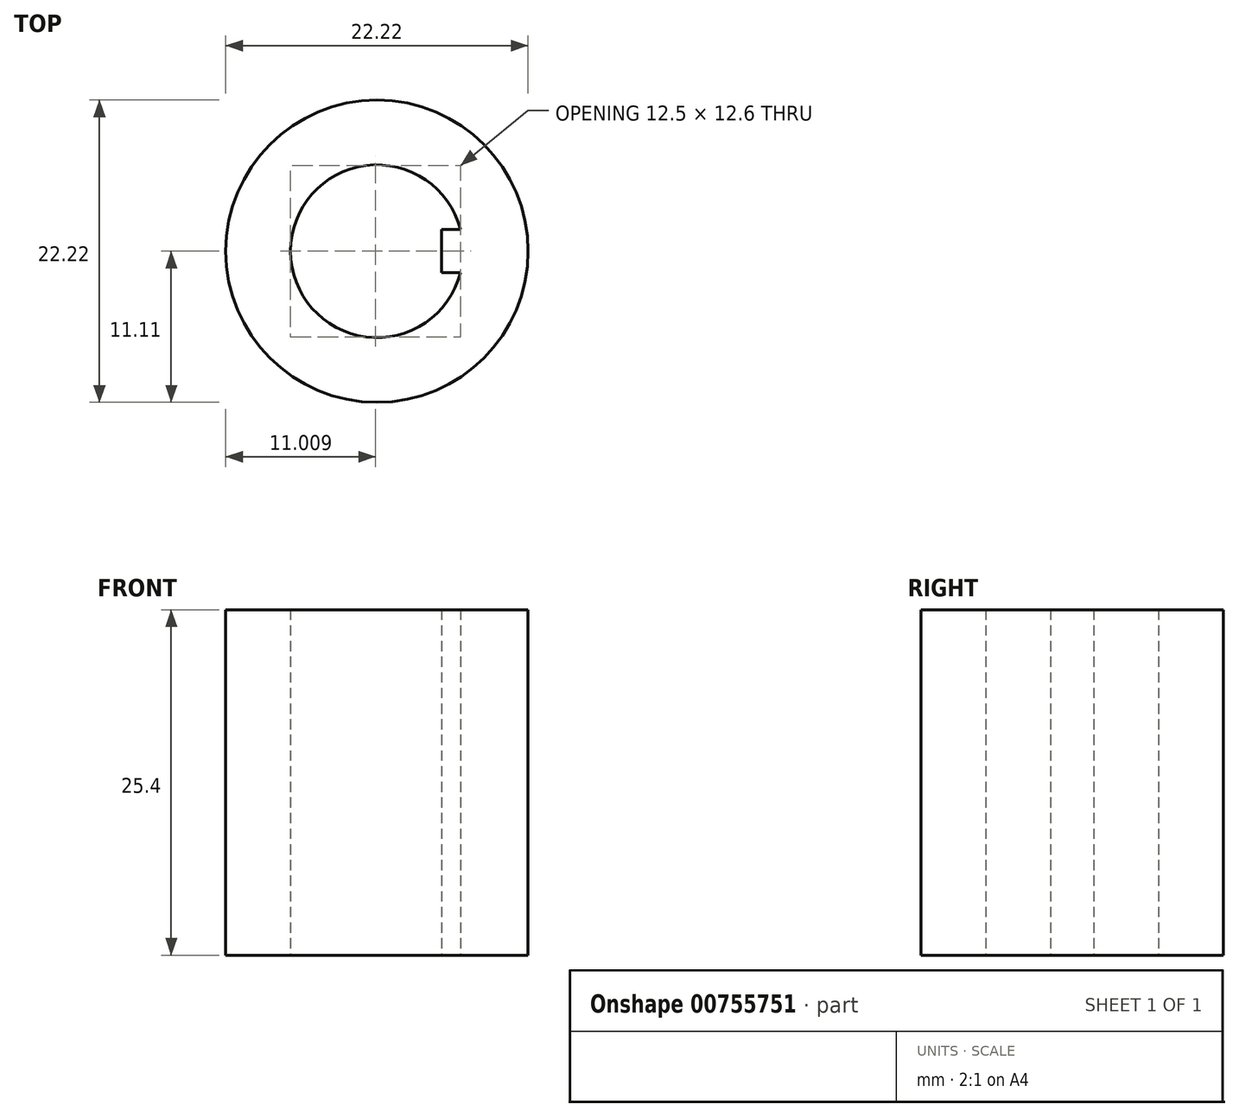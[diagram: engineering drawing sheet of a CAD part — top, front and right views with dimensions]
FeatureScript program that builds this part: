
annotation { "Feature Type Name" : "Feature", "Feature Type Description" : "" }
export const myFeature = defineFeature(function(context is Context, id is Id, definition is map)
    precondition{}
    {
        {
            var Q0;
            Q0=qCreatedBy(makeId("Top.planeOp"),FACE);
            var sketch = newSketch(context, id + "F0", { "sketchPlane" : qUnion([Q0])});
            skCircle(sketch, "E0", {"center": v(0, 0) * mm, "radius": 11.11 * mm});
            skCircle(sketch, "E1", {"center": v(0, 0) * mm, "radius": 6.35 * mm});
            skLineSegment(sketch, "E2.bottom", {"start": v(4.76, 1.59) * mm, "end": v(7.94, 1.59) * mm});
            skLineSegment(sketch, "E2.top", {"start": v(4.76, -1.59) * mm, "end": v(7.94, -1.59) * mm});
            skLineSegment(sketch, "E2.left", {"start": v(4.76, 1.59) * mm, "end": v(4.76, -1.59) * mm});
            skLineSegment(sketch, "E2.right", {"start": v(7.94, 1.59) * mm, "end": v(7.94, -1.59) * mm});
            skPoint(sketch, "E2.middle", {"position": v(6.35, 0) * mm});
            skSolve(sketch);
        }
        {
            var Q0;
            {var subQ5=sQuery(id+"F0.wireOp",EDGE,"E2.right");Q0=makeQuery(id+"F0.imprint","IMPRINT",FACE,{"disambiguationData":[TD([[makeQuery(id+"F0.imprint","IMPRINT",EDGE,{"derivedFrom":subQ5}),-1.0]])]});}
            var Q1;
            Q1=makeQuery(id+"F0.imprint","IMPRINT",FACE,{"disambiguationData":[TD([[makeQuery(id+"F0.imprint","IMPRINT",EDGE,{"derivedFrom":sQuery(id+"F0.wireOp",EDGE,"E0")}),1.0]])]});
            var Q2;
            {var subQ5=sQuery(id+"F0.wireOp",EDGE,"E2.left");Q2=makeQuery(id+"F0.imprint","IMPRINT",FACE,{"disambiguationData":[TD([[makeQuery(id+"F0.imprint","IMPRINT",EDGE,{"derivedFrom":subQ5}),1.0]])]});}
            extrude(context, id + "F1", {"entities" : qUnion([Q0, Q1, Q2]), "depth" : 25.4 * mm, "offsetDistance" : 25.4 * mm});
        }
    });
